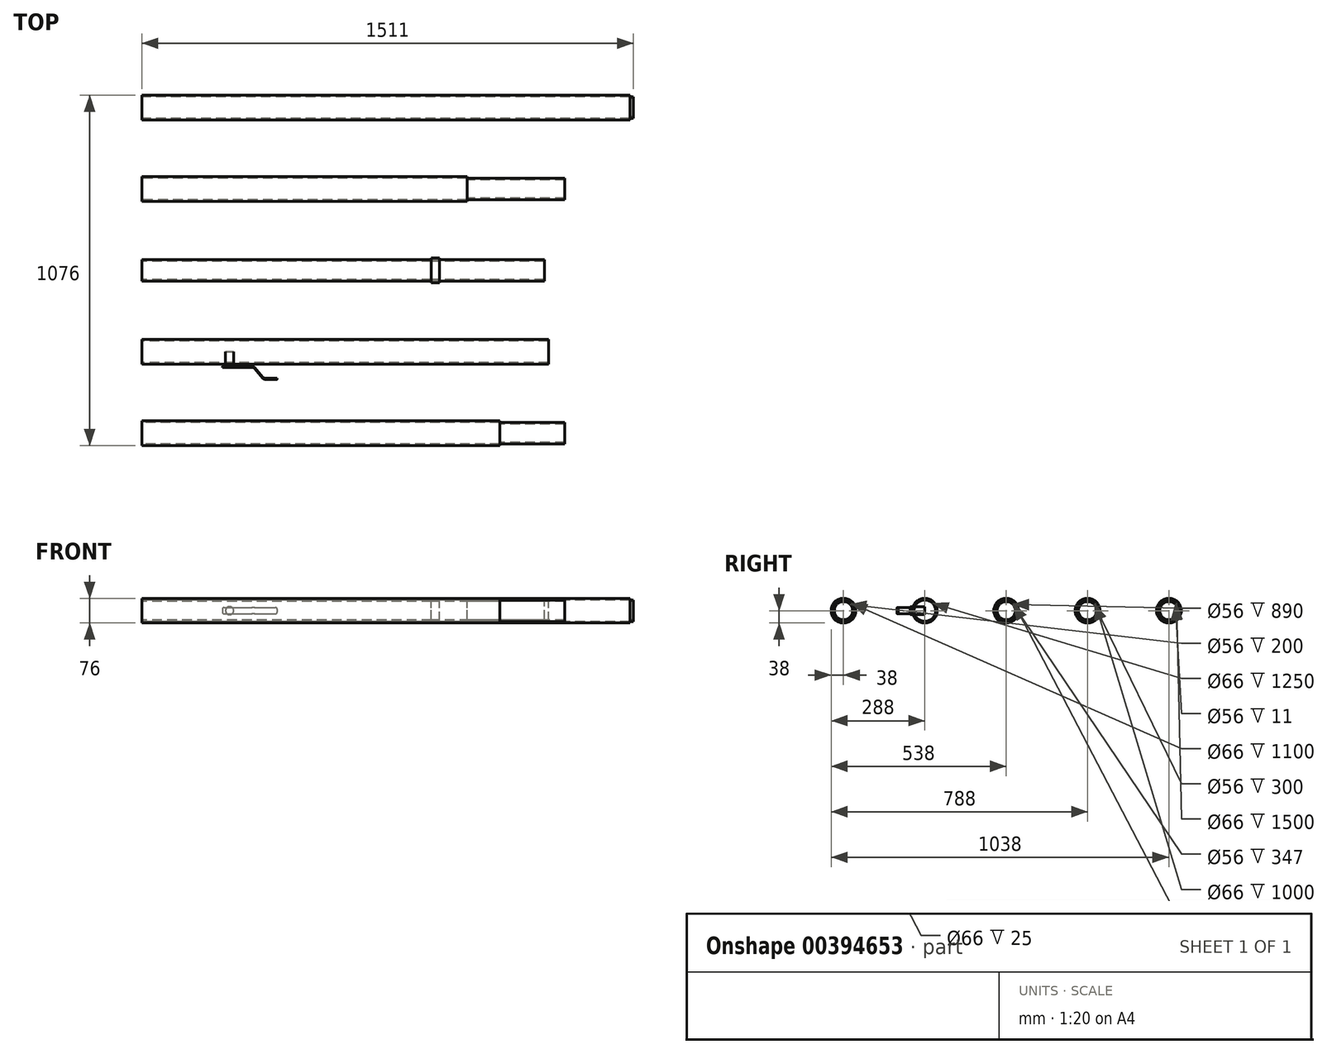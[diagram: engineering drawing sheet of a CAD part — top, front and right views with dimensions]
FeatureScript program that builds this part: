
annotation { "Feature Type Name" : "Feature", "Feature Type Description" : "" }
export const myFeature = defineFeature(function(context is Context, id is Id, definition is map)
    precondition{}
    {
        {
            var Q0;
            Q0=qCreatedBy(makeId("Right.planeOp"),FACE);
            var sketch = newSketch(context, id + "F0", { "sketchPlane" : qUnion([Q0])});
            skCircle(sketch, "E0", {"center": v(0, 0) * mm, "radius": 38 * mm});
            skCircle(sketch, "E1", {"center": v(250, 0) * mm, "radius": 38 * mm});
            skCircle(sketch, "E2", {"center": v(500, 0) * mm, "radius": 38 * mm});
            skCircle(sketch, "E3", {"center": v(-250, 0) * mm, "radius": 38 * mm});
            skCircle(sketch, "E4", {"center": v(-500, 0) * mm, "radius": 38 * mm});
            skLineSegment(sketch, "E5", {"start": v(-500, 0) * mm, "end": v(-250, 0) * mm, "construction": true});
            skLineSegment(sketch, "E6", {"start": v(-250, 0) * mm, "end": v(0, 0) * mm, "construction": true});
            skLineSegment(sketch, "E7", {"start": v(0, 0) * mm, "end": v(250, 0) * mm, "construction": true});
            skLineSegment(sketch, "E8", {"start": v(250, 0) * mm, "end": v(500, 0) * mm, "construction": true});
            skCircle(sketch, "E9.0", {"center": v(-500, 0) * mm, "radius": 33 * mm});
            skCircle(sketch, "E10.0", {"center": v(-250, 0) * mm, "radius": 33 * mm});
            skCircle(sketch, "E11.0", {"center": v(0, 0) * mm, "radius": 33 * mm});
            skCircle(sketch, "E12.0", {"center": v(250, 0) * mm, "radius": 33 * mm});
            skCircle(sketch, "E13.0", {"center": v(500, 0) * mm, "radius": 33 * mm});
            skCircle(sketch, "E14.0", {"center": v(-500, 0) * mm, "radius": 28 * mm});
            skCircle(sketch, "E15.0", {"center": v(-250, 0) * mm, "radius": 28 * mm});
            skCircle(sketch, "E16.0", {"center": v(0, 0) * mm, "radius": 28 * mm});
            skCircle(sketch, "E17.0", {"center": v(250, 0) * mm, "radius": 28 * mm});
            skCircle(sketch, "E18.0", {"center": v(500, 0) * mm, "radius": 28 * mm});
            skSolve(sketch);
        }
        {
            var Q0;
            Q0=makeQuery(id+"F0.imprint","IMPRINT",FACE,{"disambiguationData":[TD([[makeQuery(id+"F0.imprint","IMPRINT",EDGE,{"derivedFrom":sQuery(id+"F0.wireOp",EDGE,"E4")}),1.0]])]});
            extrude(context, id + "F1", {"entities" : qUnion([Q0]), "depth" : 1100 * mm, "offsetDistance" : 25 * mm});
        }
        {
            var Q0;
            Q0=makeQuery(id+"F1.opExtrude","CAP_FACE",FACE,{"disambiguationData":[OSD([sQuery(id+"F0.wireOp",EDGE,"E4"),sQuery(id+"F0.wireOp",EDGE,"E9.0")])],"isStart":false});
            var sketch = newSketch(context, id + "F2", { "sketchPlane" : qUnion([Q0])});
            skCircle(sketch, "E19.0", {"center": v(-500, 0) * mm, "radius": 28 * mm});
            skSolve(sketch);
        }
        {
            var Q0;
            Q0=makeQuery(id+"F2.imprint","IMPRINT",FACE,{"disambiguationData":[TD([[makeQuery(id+"F2.imprint","IMPRINT",EDGE,{"derivedFrom":sQuery(id+"F2.wireOp",EDGE,"E19.0")}),-1.0]])]});
            extrude(context, id + "F3", {"entities" : qUnion([Q0]), "depth" : 200 * mm, "offsetDistance" : 25 * mm});
        }
        {
            var Q0;
            Q0=makeQuery(id+"F0.imprint","IMPRINT",FACE,{"disambiguationData":[TD([[makeQuery(id+"F0.imprint","IMPRINT",EDGE,{"derivedFrom":sQuery(id+"F0.wireOp",EDGE,"E3")}),1.0]])]});
            extrude(context, id + "F4", {"entities" : qUnion([Q0]), "depth" : 1250 * mm, "offsetDistance" : 25 * mm});
        }
        {
            var Q0;
            Q0=makeQuery(id+"F0.imprint","IMPRINT",FACE,{"disambiguationData":[TD([[makeQuery(id+"F0.imprint","IMPRINT",EDGE,{"derivedFrom":sQuery(id+"F0.wireOp",EDGE,"E11.0")}),1.0]])]});
            extrude(context, id + "F5", {"entities" : qUnion([Q0]), "depth" : 890 * mm, "offsetDistance" : 25 * mm});
        }
        {
            var Q0;
            Q0=makeQuery(id+"F5.opExtrude","CAP_FACE",FACE,{"disambiguationData":[OSD([sQuery(id+"F0.wireOp",EDGE,"E11.0"),sQuery(id+"F0.wireOp",EDGE,"E16.0")])],"isStart":false});
            var sketch = newSketch(context, id + "F6", { "sketchPlane" : qUnion([Q0])});
            skCircle(sketch, "E20.0", {"center": v(0, 0) * mm, "radius": 38 * mm});
            skSolve(sketch);
        }
        {
            var Q0;
            Q0=makeQuery(id+"F6.imprint","IMPRINT",FACE,{"disambiguationData":[TD([[makeQuery(id+"F6.imprint","IMPRINT",EDGE,{"derivedFrom":sQuery(id+"F6.wireOp",EDGE,"E20.0")}),-1.0]])]});
            var Q1;
            Q1=makeQuery(id+"F6.imprint","IMPRINT",FACE,{"disambiguationData":[TD([[makeQuery(id+"F6.imprint","IMPRINT",EDGE,{"derivedFrom":sQuery(id+"F6.wireOp",EDGE,"E20.0")}),1.0]])]});
            extrude(context, id + "F7", {"entities" : qUnion([Q0, Q1]), "depth" : 25 * mm, "offsetDistance" : 25 * mm});
        }
        {
            var Q0;
            Q0=makeQuery(id+"F5.opExtrude","CAP_FACE",FACE,{"disambiguationData":[OSD([sQuery(id+"F0.wireOp",EDGE,"E11.0"),sQuery(id+"F0.wireOp",EDGE,"E16.0")])],"isStart":false});
            extrude(context, id + "F8", {"entities" : qUnion([Q0]), "depth" : 347 * mm, "offsetDistance" : 25 * mm});
        }
        {
            var Q0;
            Q0=makeQuery(id+"F0.imprint","IMPRINT",FACE,{"disambiguationData":[TD([[makeQuery(id+"F0.imprint","IMPRINT",EDGE,{"derivedFrom":sQuery(id+"F0.wireOp",EDGE,"E1")}),1.0]])]});
            extrude(context, id + "F9", {"entities" : qUnion([Q0]), "depth" : 1000 * mm, "offsetDistance" : 25 * mm});
        }
        {
            var Q0;
            Q0=makeQuery(id+"F9.opExtrude","CAP_FACE",FACE,{"disambiguationData":[OSD([sQuery(id+"F0.wireOp",EDGE,"E1"),sQuery(id+"F0.wireOp",EDGE,"E12.0")])],"isStart":false});
            var sketch = newSketch(context, id + "F10", { "sketchPlane" : qUnion([Q0])});
            skCircle(sketch, "E21.0", {"center": v(250, 0) * mm, "radius": 28 * mm});
            skSolve(sketch);
        }
        {
            var Q0;
            Q0=makeQuery(id+"F10.imprint","IMPRINT",FACE,{"disambiguationData":[TD([[makeQuery(id+"F10.imprint","IMPRINT",EDGE,{"derivedFrom":sQuery(id+"F10.wireOp",EDGE,"E21.0")}),-1.0]])]});
            extrude(context, id + "F11", {"entities" : qUnion([Q0]), "depth" : 300 * mm, "offsetDistance" : 25 * mm});
        }
        {
            var Q0;
            Q0=makeQuery(id+"F0.imprint","IMPRINT",FACE,{"disambiguationData":[TD([[makeQuery(id+"F0.imprint","IMPRINT",EDGE,{"derivedFrom":sQuery(id+"F0.wireOp",EDGE,"E2")}),1.0]])]});
            extrude(context, id + "F12", {"entities" : qUnion([Q0]), "depth" : 1500 * mm, "offsetDistance" : 25 * mm});
        }
        {
            var Q0;
            Q0=makeQuery(id+"F12.opExtrude","CAP_FACE",FACE,{"disambiguationData":[OSD([sQuery(id+"F0.wireOp",EDGE,"E2"),sQuery(id+"F0.wireOp",EDGE,"E13.0")])],"isStart":false});
            var sketch = newSketch(context, id + "F13", { "sketchPlane" : qUnion([Q0])});
            skCircle(sketch, "E22.0", {"center": v(500, 0) * mm, "radius": 28 * mm});
            skSolve(sketch);
        }
        {
            var Q0;
            Q0=makeQuery(id+"F13.imprint","IMPRINT",FACE,{"disambiguationData":[TD([[makeQuery(id+"F13.imprint","IMPRINT",EDGE,{"derivedFrom":sQuery(id+"F13.wireOp",EDGE,"E22.0")}),-1.0]])]});
            extrude(context, id + "F14", {"entities" : qUnion([Q0]), "depth" : 11 * mm, "offsetDistance" : 25 * mm});
        }
        {
            var Q0;
            Q0=qCreatedBy(makeId("Front.planeOp"),FACE);
            var Q1;
            Q1=sQuery(id+"F0.wireOp",VERTEX,"E5.end");
            cPlane(context, id + "F15", {"entities" : qUnion([Q0, Q1]), "cplaneType" : CPlaneType.PLANE_POINT, "offset" : 25 * mm, "width" : 150 * mm, "height" : 150 * mm});
        }
        {
            var Q0;
            Q0=qCreatedBy(id+"F15.planeOp",FACE);
            var sketch = newSketch(context, id + "F16", { "sketchPlane" : qUnion([Q0])});
            skCircle(sketch, "E23", {"center": v(270, 0) * mm, "radius": 12.5 * mm});
            skLineSegment(sketch, "E24", {"start": v(0, 0) * mm, "end": v(270, 0) * mm, "construction": true});
            skSolve(sketch);
        }
        {
            var Q0;
            Q0=makeQuery(id+"F16.imprint","IMPRINT",FACE,{"disambiguationData":[TD([[makeQuery(id+"F16.imprint","IMPRINT",EDGE,{"derivedFrom":sQuery(id+"F16.wireOp",EDGE,"E23")}),1.0]])]});
            extrude(context, id + "F17", {"entities" : qUnion([Q0]), "depth" : 45 * mm, "offsetDistance" : 25 * mm});
        }
        {
            var Q0;
            Q0=qCreatedBy(makeId("Top.planeOp"),FACE);
            var sketch = newSketch(context, id + "F18", { "sketchPlane" : qUnion([Q0])});
            skLineSegment(sketch, "E25.bottom", {"start": v(248.13, -295) * mm, "end": v(343.7, -295) * mm});
            skLineSegment(sketch, "E25.top", {"start": v(248.13, -298) * mm, "end": v(342.33, -298) * mm});
            skLineSegment(sketch, "E25.left", {"start": v(248.13, -295) * mm, "end": v(248.13, -298) * mm});
            skLineSegment(sketch, "E26.bottom", {"start": v(343.7, -295) * mm, "end": v(375.85, -331.98) * mm});
            skLineSegment(sketch, "E26.top", {"start": v(342.33, -298) * mm, "end": v(374.48, -334.98) * mm});
            skLineSegment(sketch, "E27.bottom", {"start": v(374.48, -334.98) * mm, "end": v(415.77, -334.98) * mm});
            skLineSegment(sketch, "E27.top", {"start": v(375.85, -331.98) * mm, "end": v(415.77, -331.98) * mm});
            skLineSegment(sketch, "E27.right", {"start": v(415.77, -334.98) * mm, "end": v(415.77, -331.98) * mm});
            skLineSegment(sketch, "E28", {"start": v(400.77, -334.98) * mm, "end": v(400.77, -384.76) * mm});
            skLineSegment(sketch, "E29", {"start": v(396.77, -334.98) * mm, "end": v(393.77, -381.81) * mm});
            skArc(sketch, "E30", {"start": v(393.77, -381.81) * mm, "mid": v(396.9, -384.19) * mm, "end": v(400.77, -384.76) * mm});
            skSolve(sketch);
        }
        {
            var Q0;
            Q0=sQuery(id+"F18.wireOp",EDGE,"E29");
            var Q1;
            Q1=sQuery(id+"F18.wireOp",EDGE,"E30");
            var Q2;
            Q2=sQuery(id+"F18.wireOp",EDGE,"E28");
            revolve(context, id + "F19", {"bodyType" : ToolBodyType.SURFACE, "surfaceOperationType" : NewSurfaceOperationType.NEW, "surfaceEntities" : qUnion([Q0, Q1]), "axis" : qUnion([Q2]), "revolveType" : RevolveType.FULL});
        }
        {
            var Q0;
            Q0=makeQuery(id+"F18.imprint","IMPRINT",FACE,{"disambiguationData":[TD([[makeQuery(id+"F18.imprint","IMPRINT",EDGE,{"derivedFrom":sQuery(id+"F18.wireOp",EDGE,"E25.bottom")}),-1.0]])]});
            extrude(context, id + "F20", {"entities" : qUnion([Q0]), "operationType" : NewBodyOperationType.ADD, "endBound" : BoundingType.SYMMETRIC, "depth" : 20 * mm, "offsetDistance" : 25 * mm});
        }
        {
            var Q0;
            Q0=makeQuery(id+"F20.opExtrude","CAP_EDGE",EDGE,{"disambiguationData":[OSD([sQuery(id+"F18.wireOp",EDGE,"E27.right")])],"isStart":false});
            var Q1;
            Q1=makeQuery(id+"F20.opExtrude","CAP_EDGE",EDGE,{"disambiguationData":[OSD([sQuery(id+"F18.wireOp",EDGE,"E27.right")])],"isStart":true});
            var Q2;
            Q2=makeQuery(id+"F19.opRevolve","SWEPT_EDGE",EDGE,{"disambiguationData":[OSD([sQuery(id+"F18.wireOp",VERTEX,"E30.start")])]});
            var Q3;
            Q3=makeQuery(id+"F20.opExtrude","CAP_EDGE",EDGE,{"disambiguationData":[OSD([sQuery(id+"F18.wireOp",EDGE,"E25.left")])],"isStart":false});
            var Q4;
            Q4=makeQuery(id+"F20.opExtrude","CAP_EDGE",EDGE,{"disambiguationData":[OSD([sQuery(id+"F18.wireOp",EDGE,"E25.left")])],"isStart":true});
            fillet(context, id + "F21", {"entities" : qUnion([Q0, Q1, Q2, Q3, Q4]), "tangentPropagation" : true, "radius" : 5 * mm, "defaultsChanged" : false, "vertexSettings" : [], "allowEdgeOverflow" : false});
        }
        {
            var Q0;
            Q0=makeQuery(id+"F20.opExtrude","SWEPT_EDGE",EDGE,{"disambiguationData":[OSD([sQuery(id+"F18.wireOp",EDGE,"E25.top"),sQuery(id+"F18.wireOp",EDGE,"E26.top")])]});
            var Q1;
            Q1=makeQuery(id+"F20.opExtrude","SWEPT_EDGE",EDGE,{"disambiguationData":[OSD([sQuery(id+"F18.wireOp",EDGE,"E26.top"),sQuery(id+"F18.wireOp",EDGE,"E27.bottom")])]});
            var Q2;
            Q2=makeQuery(id+"F20.opExtrude","SWEPT_EDGE",EDGE,{"disambiguationData":[OSD([sQuery(id+"F18.wireOp",EDGE,"E26.bottom"),sQuery(id+"F18.wireOp",EDGE,"E27.top")])]});
            var Q3;
            Q3=makeQuery(id+"F20.opExtrude","SWEPT_EDGE",EDGE,{"disambiguationData":[OSD([sQuery(id+"F18.wireOp",EDGE,"E25.bottom"),sQuery(id+"F18.wireOp",EDGE,"E26.bottom")])]});
            fillet(context, id + "F22", {"entities" : qUnion([Q0, Q1, Q2, Q3]), "tangentPropagation" : true, "radius" : 10 * mm, "defaultsChanged" : true, "vertexSettings" : [], "allowEdgeOverflow" : false});
        }
    });
